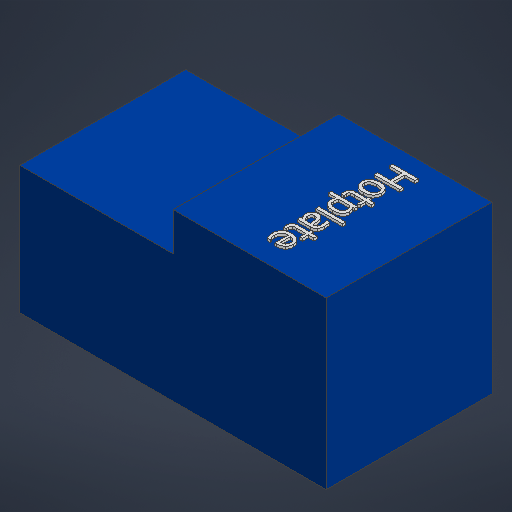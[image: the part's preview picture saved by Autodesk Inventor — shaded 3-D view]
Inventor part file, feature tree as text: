
AUTODESK INVENTOR PART (.ipt)
format: ipt  version: 2025.1 (Build 291241000, 241)  size: 345,088 bytes
history: native  units: mm
features: extrude x3, sketch x2
ambient origin geometry x8: Origin, YZ Plane, XZ Plane, XY Plane, X Axis, Y Axis, Z Axis, Center Point
bodies: Solid1 (feature_tree)
feature tree (5):
  sketch  "Sketch1"  dims[d0=240.0mm d1=130.0mm]
  extrude  "Extrusion1"  Depth=130.0mm
  extrude  "Extrusion2"  Depth=120.0mm
  extrude  "Extrusion3"  Depth=30.0mm TaperAngle=0.0deg
  sketch  "Sketch2"  dims[d2=100.0mm d3=0.0mm d4=120.0mm d5=30.0mm d6=0.0mm d7=2.0mm d8=0.0mm]
